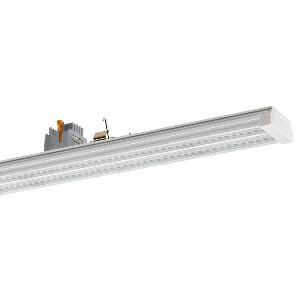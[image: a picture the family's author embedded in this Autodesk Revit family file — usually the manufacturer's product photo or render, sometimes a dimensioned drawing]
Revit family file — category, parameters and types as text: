
# Revit family: conveo_-_cvg_15000_850_xn-l_da_7_226848429-00804981_c46d
name_source: partatom
category: Lighting Fixtures
units: mm (PartAtom-declared; Revit-internal decimal feet)

## family parameters
Cut with Voids When Loaded = No
Host = Face
Light Source = No
Part Type = Normal
Room Calculation Point = No
Round Connector Dimension = Use Diameter
Shared = No

## types (1)
- CONVEO - CVG 15000/850/xN-L/DA/7 (1 x LED, 15400 lm, 5000K)
    Apparent Load = 95 VA
    Approval mark = CE
    CIE Flux Codes = 86 95 99 100 100
    Color Rendering = 80-89
    Color Temperature = 5000K
    Control Gear = Electronic ballast
    Default Elevation = 1800 mm
    Description = CVG 15000/850/xN-L/DA/7|Continuous-row system|light source: LED|work equipment: Adjustable electronic ballast, digital DALI|connected load: 220-240 V, 50-60 Hz|Power consumption: approx. 95 W|luminous flux: 15400 lm|luminous efficacy: 162 lm/W|colour temperature: Cold white, ca. 5000 K|color rendering index (CRI): >= 80|chromaticity tolerance:  3 SDCM|System of protection: IP 54|class of protection: I|technology: Continuously dimmable|luminaire body|material: Aluminium|surface: Powder coatet|colour: White|lamp cover: Acrylic (PMMA), Satine|weight (net): approx. 2.2 kg|Fastening: Available separately|maximum ambient temperature: 41 ░C|glare control: Lens optics|Approval mark: VDE - ENEC|
    Frequency = 50 Hz
    Height = 70 mm
    Lamp = 1 x LED
    Lamp Light Flux = 15400 lm
    Lamp count = 1
    Length = 1500 mm
    Luminous efficacy = 162 lm/W
    Manufacturer = Waldmann
    ModVariant = No
    Model = 226848429-00804981
    Mounting Place = Ceiling
    Mounting Type = Pendant
    Number of Poles = 1
    OnlyDefault = Yes
    Power Factor = 1
    Product Name = CONVEO - CVG 15000/850/xN-L/DA/7
    Product group = Continuous-row system (industry)
    ProductGroupID = 301
    Protection Class = Protection class I
    Protection Degree = IP 54
    RLX_Detail_Level = 1
    RlxData = <blob elided: 135457 chars, md5=e735f5e5>
    Socket = socket
    Standby Power = 0 W
    System Light Flux = 15400 lm
    System Power = 95 W
    Type Comments = Product without accessories
    Type Image = 226848299-00804968_2l7.jpg
    URL = http://relux.com
    VarID = ---
    Voltage = 230 V
    Voltage Range = 220-240 V
    Weight = 0.00 kg
    Width = 64 mm

## geometry (parser evidence)
native form markers: Blend x4, Sweep x10
no freeform markers — native parametric forms only
